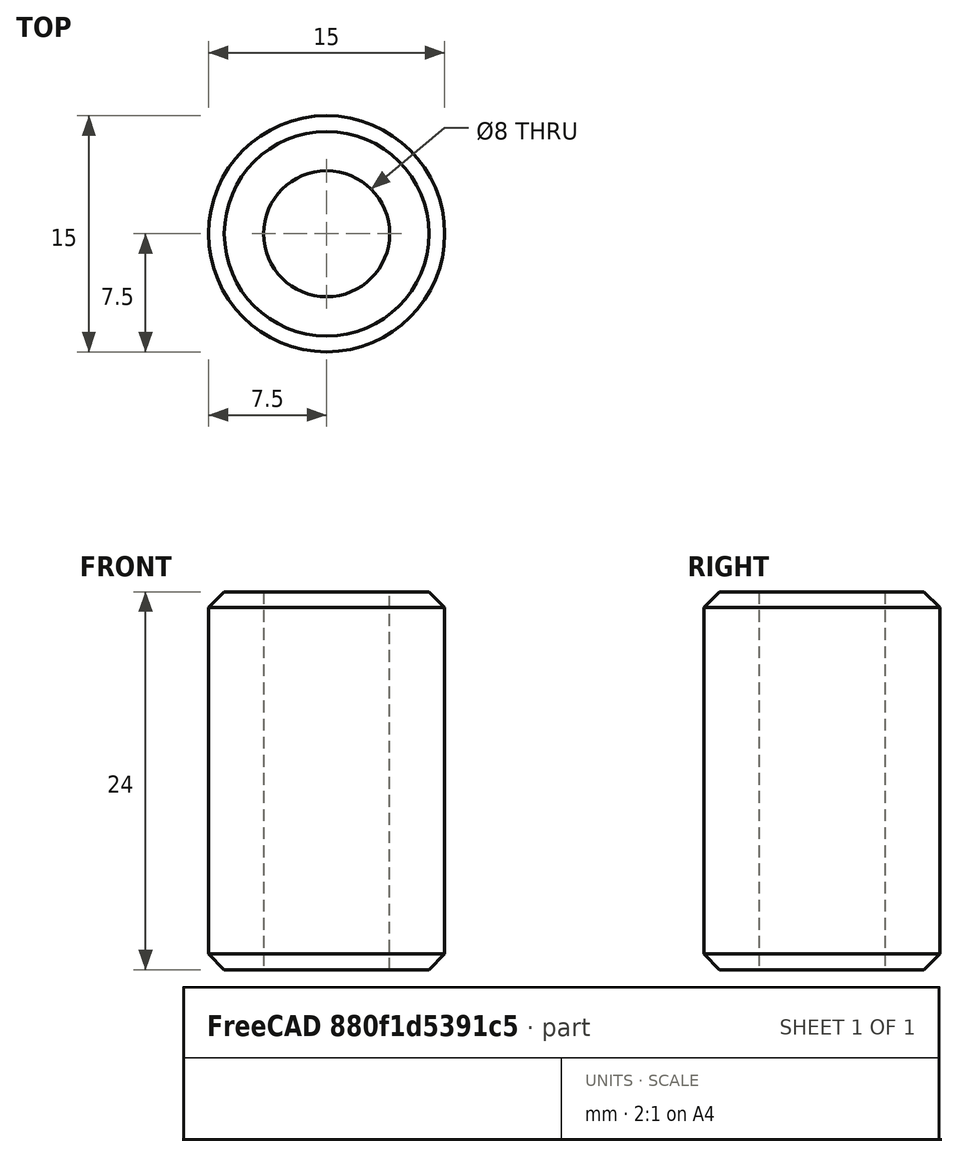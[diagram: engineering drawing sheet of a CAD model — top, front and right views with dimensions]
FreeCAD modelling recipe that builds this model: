
FCSTD DOCUMENT  (FreeCAD 0.16RUnknown)
Label: linearBearing-lm8uu
License: All rights reserved
LicenseURL: http://en.wikipedia.org/wiki/All_rights_reserved
objects: PartDesign::Chamfer×2, Sketcher::SketchObject×1, PartDesign::Pad×1
note: 5 computed .brp shape members not serialized (recipe doc carries the construction recipe); baked Part::Feature solids carry a one-line shape summary decoded from their .brp

FEATURE [Sketcher::SketchObject] Sketch
  sketch-geometry (2):
    g0: Circle CenterX=0 CenterY=0 CenterZ=0 NormalX=0 NormalY=0 NormalZ=1 Radius=7.5
    g1: Circle CenterX=0 CenterY=0 CenterZ=0 NormalX=0 NormalY=0 NormalZ=1 Radius=4
  constraints (4):
    c: Coincident(g1,g0)
    c: Radius(g1) = 4
    c: Radius(g0) = 7.5
    c: Coincident(g0,g-1)
FEATURE [PartDesign::Pad] Pad
  Length = 24
  Length2 = 100
  Sketch = -> Sketch
  Type = 0
FEATURE [PartDesign::Chamfer] Chamfer
  Base = -> Pad [Edge3]
  Size = 1
FEATURE [PartDesign::Chamfer] Chamfer001
  Base = -> Chamfer [Edge3]
  Size = 1
